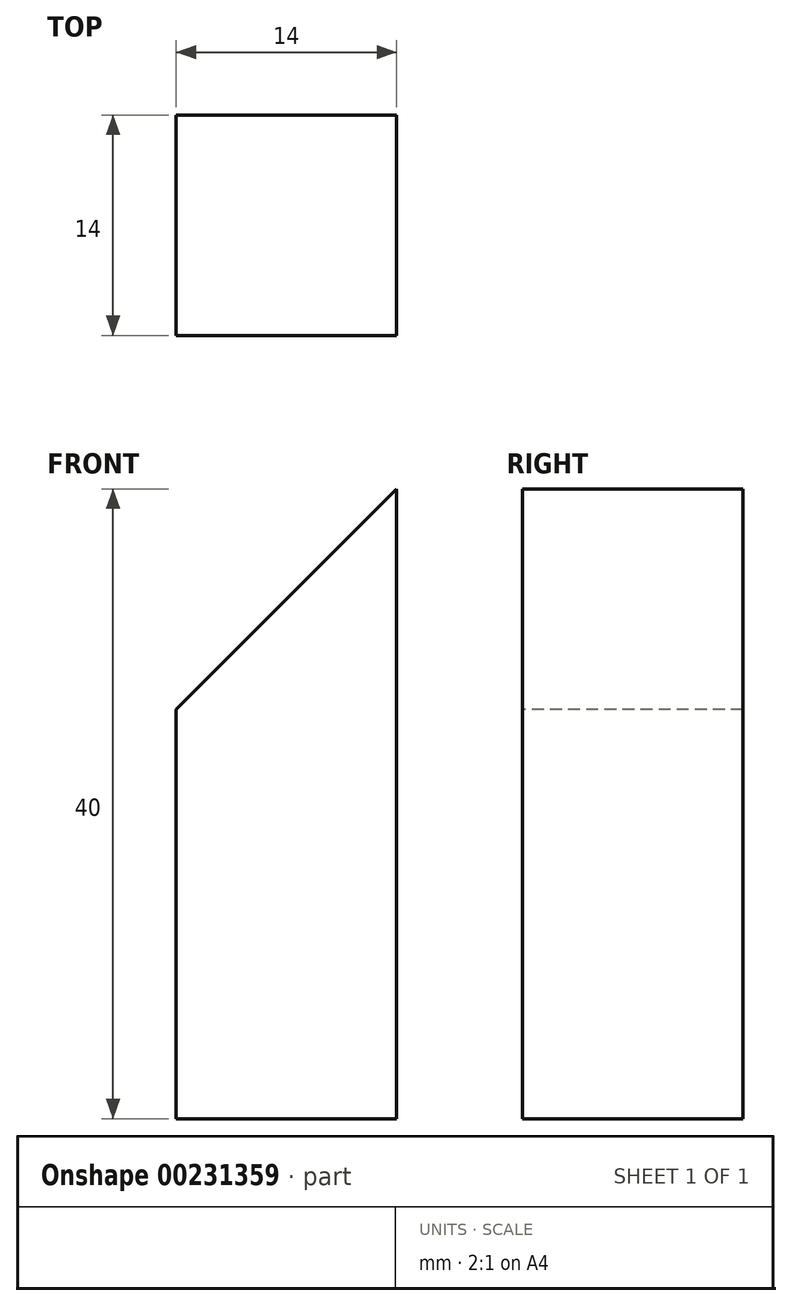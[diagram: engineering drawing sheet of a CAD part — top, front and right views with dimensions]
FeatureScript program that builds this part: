
annotation { "Feature Type Name" : "Feature", "Feature Type Description" : "" }
export const myFeature = defineFeature(function(context is Context, id is Id, definition is map)
    precondition{}
    {
        {
            var Q0;
            Q0=qCreatedBy(makeId("Top.planeOp"),FACE);
            var sketch = newSketch(context, id + "F0", { "sketchPlane" : qUnion([Q0])});
            skLineSegment(sketch, "E0.bottom", {"start": v(7, -7) * mm, "end": v(-7, -7) * mm});
            skLineSegment(sketch, "E0.top", {"start": v(7, 7) * mm, "end": v(-7, 7) * mm});
            skLineSegment(sketch, "E0.left", {"start": v(7, -7) * mm, "end": v(7, 7) * mm});
            skLineSegment(sketch, "E0.right", {"start": v(-7, -7) * mm, "end": v(-7, 7) * mm});
            skPoint(sketch, "E0.middle", {"position": v(0, 0) * mm});
            skSolve(sketch);
        }
        {
            var Q0;
            Q0 = qSketchRegion(id + "F0", true);
            extrude(context, id + "F1", {"entities" : qUnion([Q0]), "depth" : 40 * mm});
        }
        {
            var Q0;
            Q0=makeQuery(id+"F1.opExtrude","SWEPT_FACE",FACE,{"disambiguationData":[OSD([sQuery(id+"F0.wireOp",EDGE,"E0.bottom")])]});
            var sketch = newSketch(context, id + "F2", { "sketchPlane" : qUnion([Q0])});
            skLineSegment(sketch, "E1", {"start": v(7, 40) * mm, "end": v(-7, 26) * mm});
            skLineSegment(sketch, "E2", {"start": v(-7, 26) * mm, "end": v(-7, 40) * mm});
            skLineSegment(sketch, "E3", {"start": v(-7, 40) * mm, "end": v(7, 40) * mm});
            skSolve(sketch);
        }
        {
            var Q0;
            Q0 = qSketchRegion(id + "F2", true);
            extrude(context, id + "F3", {"entities" : qUnion([Q0]), "operationType" : NewBodyOperationType.REMOVE, "oppositeDirection" : true, "depth" : 25 * mm});
        }
    });
